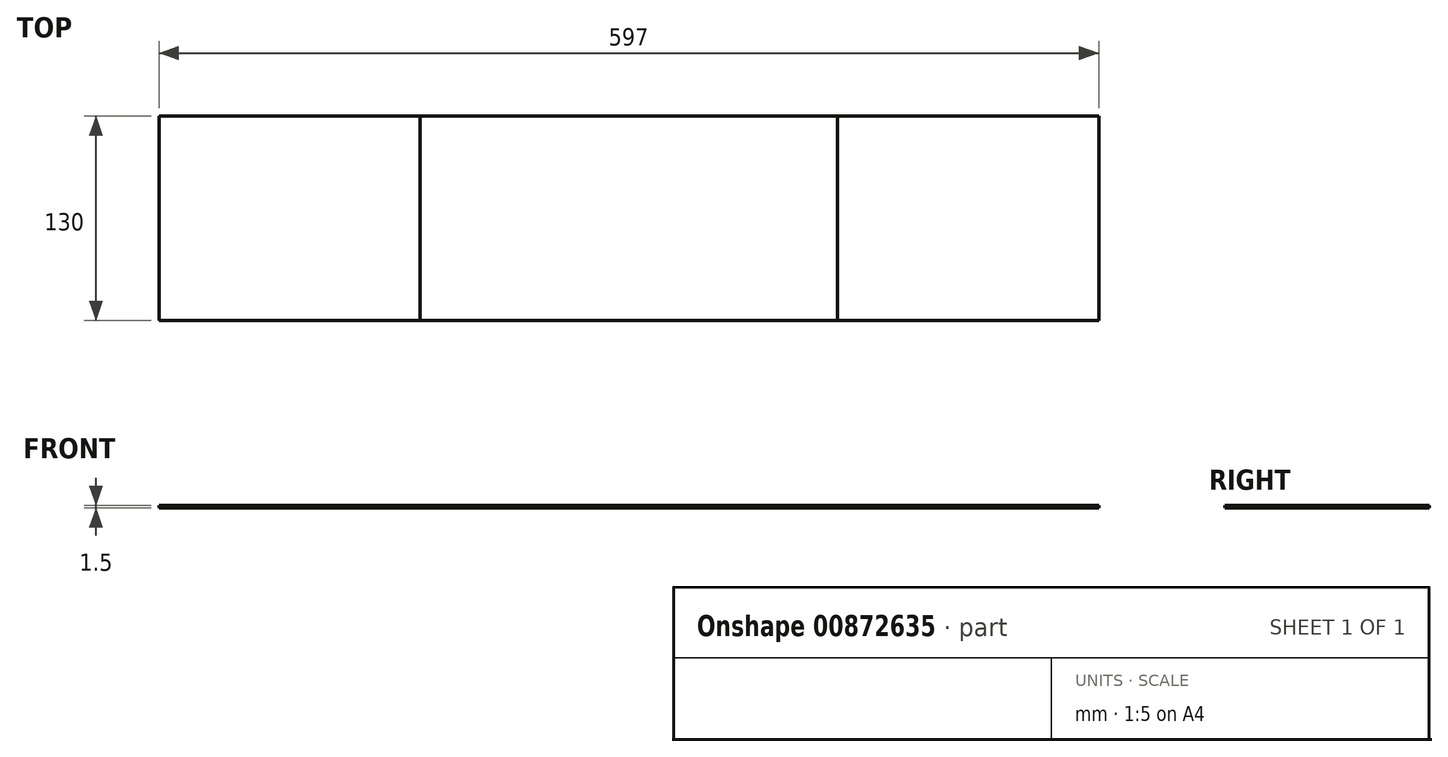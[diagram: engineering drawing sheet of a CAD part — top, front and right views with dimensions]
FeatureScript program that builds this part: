
annotation { "Feature Type Name" : "Feature", "Feature Type Description" : "" }
export const myFeature = defineFeature(function(context is Context, id is Id, definition is map)
    precondition{}
    {
        {
            var Q0;
            Q0=qCreatedBy(makeId("Top.planeOp"),FACE);
            var sketch = newSketch(context, id + "F0", { "sketchPlane" : qUnion([Q0])});
            skLineSegment(sketch, "E0.bottom", {"start": v(-464.89, -31.66) * mm, "end": v(-298.89, -31.66) * mm});
            skLineSegment(sketch, "E0.top", {"start": v(-464.89, -161.66) * mm, "end": v(-298.89, -161.66) * mm});
            skLineSegment(sketch, "E0.left", {"start": v(-464.89, -31.66) * mm, "end": v(-464.89, -161.66) * mm});
            skLineSegment(sketch, "E0.right", {"start": v(-298.89, -31.66) * mm, "end": v(-298.89, -161.66) * mm});
            skSolve(sketch);
        }
        {
            var Q0;
            Q0=qCreatedBy(makeId("Top.planeOp"),FACE);
            var sketch = newSketch(context, id + "F1", { "sketchPlane" : qUnion([Q0])});
            skLineSegment(sketch, "E1.bottom", {"start": v(-298.89, -31.66) * mm, "end": v(-33.89, -31.66) * mm});
            skLineSegment(sketch, "E1.top", {"start": v(-298.89, -161.66) * mm, "end": v(-33.89, -161.66) * mm});
            skLineSegment(sketch, "E1.left", {"start": v(-298.89, -31.66) * mm, "end": v(-298.89, -161.66) * mm});
            skLineSegment(sketch, "E1.right", {"start": v(-33.89, -31.66) * mm, "end": v(-33.89, -161.66) * mm});
            skSolve(sketch);
        }
        {
            var Q0;
            Q0=qCreatedBy(makeId("Top.planeOp"),FACE);
            var sketch = newSketch(context, id + "F2", { "sketchPlane" : qUnion([Q0])});
            skLineSegment(sketch, "E2.bottom", {"start": v(-33.89, -31.66) * mm, "end": v(132.11, -31.66) * mm});
            skLineSegment(sketch, "E2.top", {"start": v(-33.89, -161.66) * mm, "end": v(132.11, -161.66) * mm});
            skLineSegment(sketch, "E2.left", {"start": v(-33.89, -31.66) * mm, "end": v(-33.89, -161.66) * mm});
            skLineSegment(sketch, "E2.right", {"start": v(132.11, -31.66) * mm, "end": v(132.11, -161.66) * mm});
            skSolve(sketch);
        }
        {
            var Q0;
            Q0=makeQuery(id+"F0.imprint","IMPRINT",FACE,{"disambiguationData":[TD([[makeQuery(id+"F0.imprint","IMPRINT",EDGE,{"derivedFrom":sQuery(id+"F0.wireOp",EDGE,"E0.bottom")}),-1.0]])]});
            var Q1;
            Q1=makeQuery(id+"F1.imprint","IMPRINT",FACE,{"disambiguationData":[TD([[makeQuery(id+"F1.imprint","IMPRINT",EDGE,{"derivedFrom":sQuery(id+"F1.wireOp",EDGE,"E1.bottom")}),-1.0]])]});
            var Q2;
            Q2=makeQuery(id+"F2.imprint","IMPRINT",FACE,{"disambiguationData":[TD([[makeQuery(id+"F2.imprint","IMPRINT",EDGE,{"derivedFrom":sQuery(id+"F2.wireOp",EDGE,"E2.bottom")}),-1.0]])]});
            extrude(context, id + "F3", {"entities" : qUnion([Q0, Q1, Q2]), "depth" : 1.5 * mm, "offsetDistance" : 25 * mm});
        }
    });
